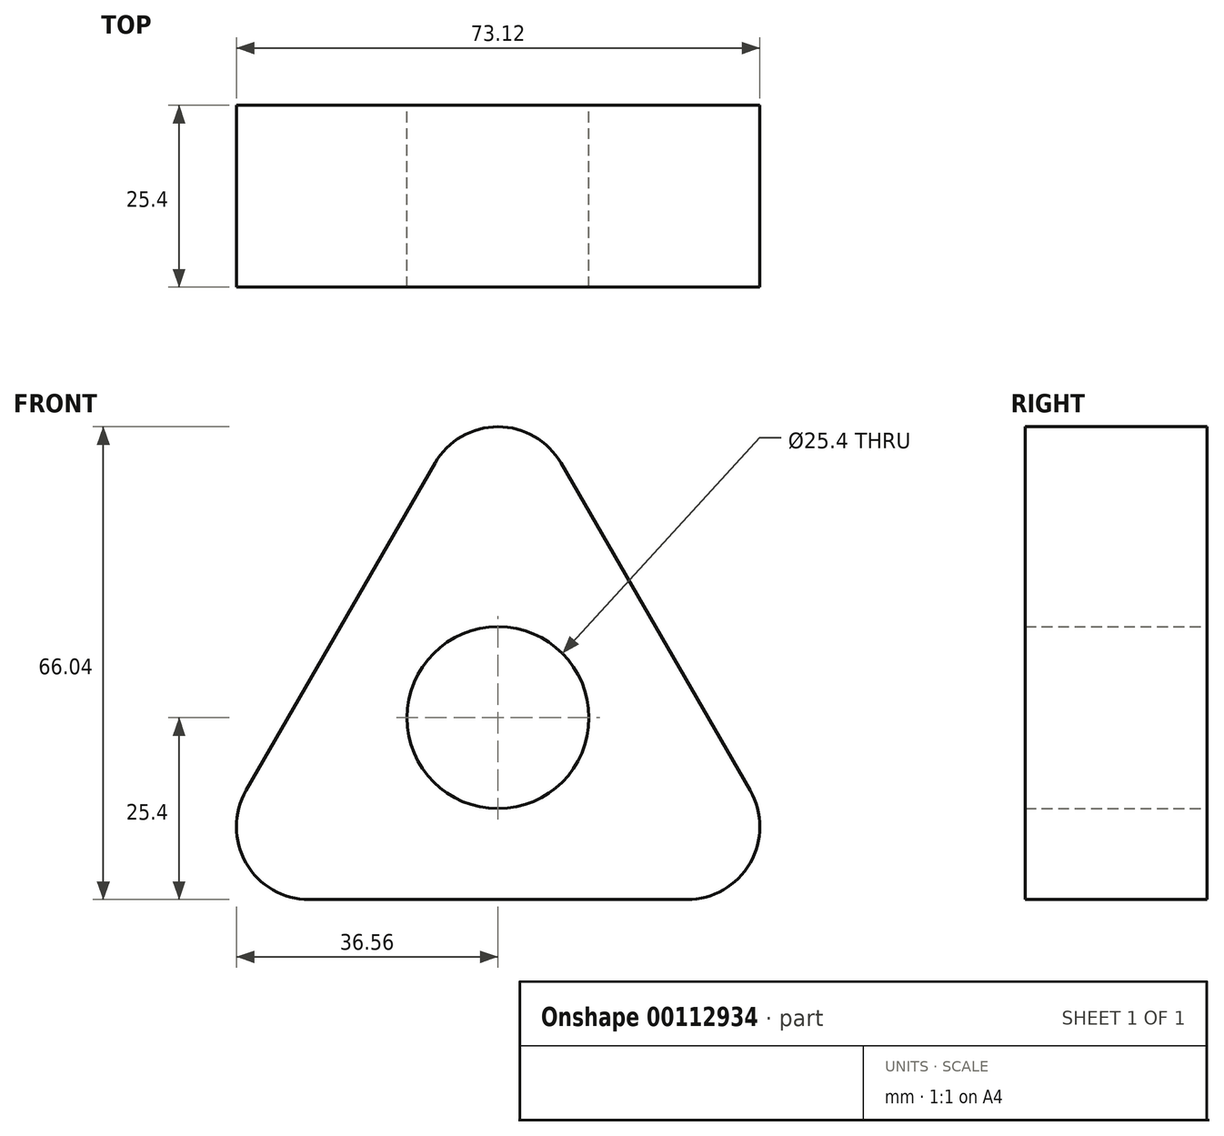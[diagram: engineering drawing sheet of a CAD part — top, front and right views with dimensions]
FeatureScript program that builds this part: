
annotation { "Feature Type Name" : "Feature", "Feature Type Description" : "" }
export const myFeature = defineFeature(function(context is Context, id is Id, definition is map)
    precondition{}
    {
        {
            var Q0;
            Q0=qCreatedBy(makeId("Front.planeOp"),FACE);
            var sketch = newSketch(context, id + "F0", { "sketchPlane" : qUnion([Q0])});
            skCircle(sketch, "E0", {"center": v(0, 0) * mm, "radius": 12.7 * mm});
            skLineSegment(sketch, "E1", {"start": v(0, 0) * mm, "end": v(0, 50.8) * mm, "construction": true});
            skLineSegment(sketch, "E2", {"start": v(0, 0) * mm, "end": v(44, -25.4) * mm, "construction": true});
            skLineSegment(sketch, "E3", {"start": v(0, 0) * mm, "end": v(-44, -25.4) * mm, "construction": true});
            skLineSegment(sketch, "E4", {"start": v(-44, -25.4) * mm, "end": v(0, 50.8) * mm});
            skLineSegment(sketch, "E5", {"start": v(-44, -25.4) * mm, "end": v(44, -25.4) * mm});
            skLineSegment(sketch, "E6", {"start": v(44, -25.4) * mm, "end": v(0, 50.8) * mm});
            skSolve(sketch);
        }
        {
            var Q0;
            Q0 = qSketchRegion(id + "F0", true);
            extrude(context, id + "F1", {"entities" : qUnion([Q0]), "endBound" : BoundingType.SYMMETRIC, "depth" : 25.4 * mm});
        }
        {
            var Q0;
            Q0=makeQuery(id+"F1.opExtrude","SWEPT_EDGE",EDGE,{"disambiguationData":[OSD([sQuery(id+"F0.wireOp",EDGE,"E4"),sQuery(id+"F0.wireOp",EDGE,"E5")])]});
            var Q1;
            Q1=makeQuery(id+"F1.opExtrude","SWEPT_EDGE",EDGE,{"disambiguationData":[OSD([sQuery(id+"F0.wireOp",EDGE,"E5"),sQuery(id+"F0.wireOp",EDGE,"E6")])]});
            var Q2;
            Q2=makeQuery(id+"F1.opExtrude","SWEPT_EDGE",EDGE,{"disambiguationData":[OSD([sQuery(id+"F0.wireOp",EDGE,"E4"),sQuery(id+"F0.wireOp",EDGE,"E6")])]});
            fillet(context, id + "F2", {"entities" : qUnion([Q0, Q1, Q2]), "radius" : 10.16 * mm, "tangentPropagation" : true, "allowEdgeOverflow" : false});
        }
    });
